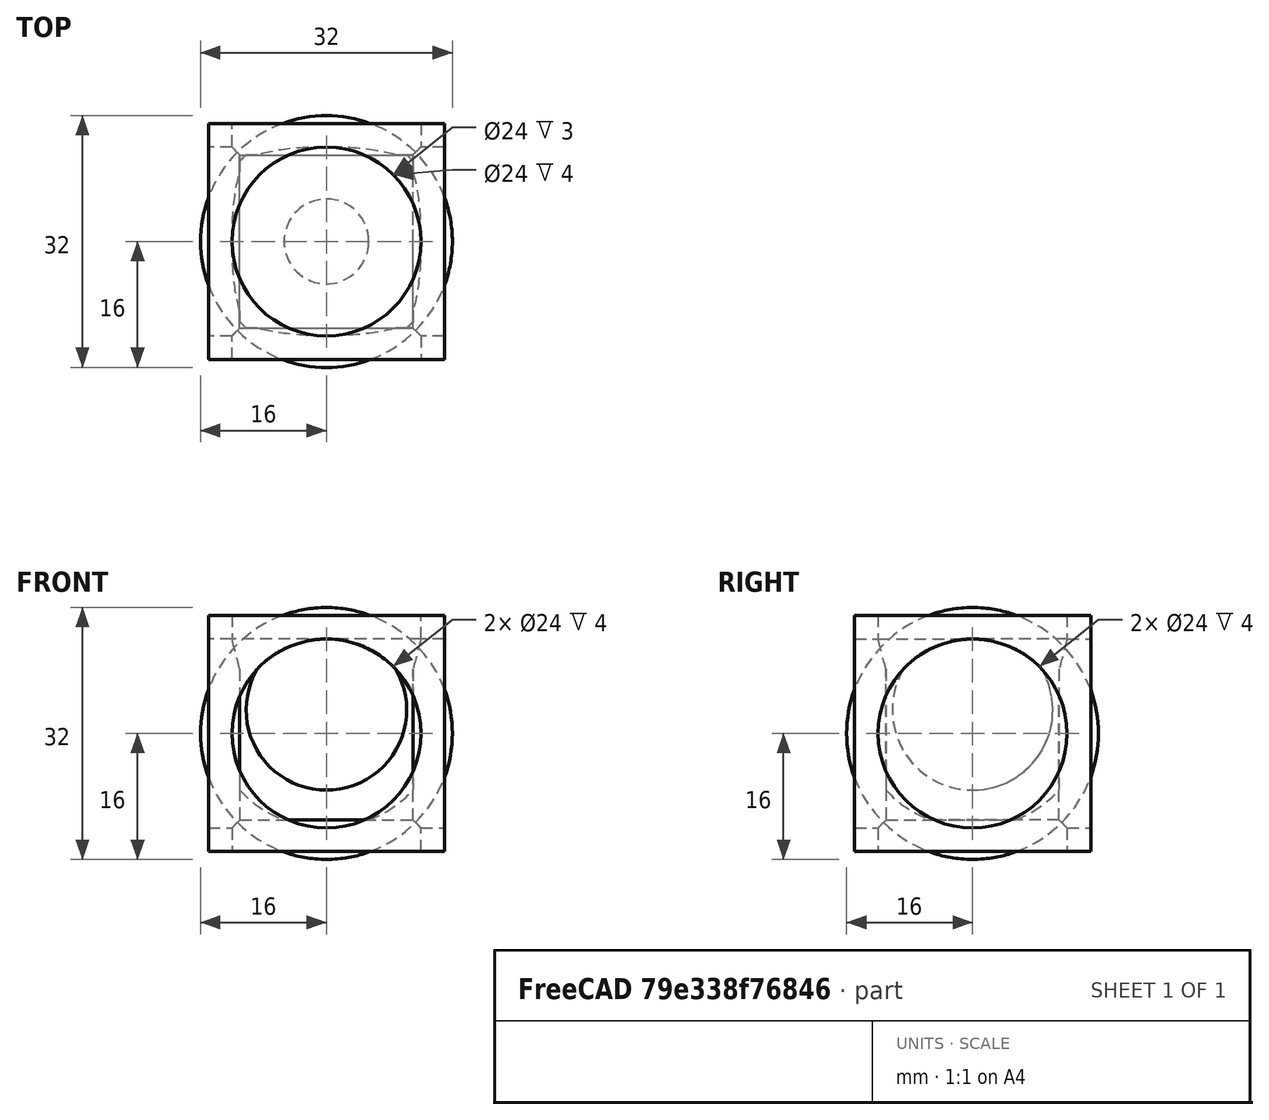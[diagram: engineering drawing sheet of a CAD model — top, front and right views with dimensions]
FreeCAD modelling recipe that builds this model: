
FCSTD DOCUMENT  (FreeCAD 0.20R29603 (Git))
Label: Ielkadi_repte3
License: All rights reserved
LicenseURL: http://en.wikipedia.org/wiki/All_rights_reserved
objects: Part::Cut×7, Part::Cylinder×6, Part::Sphere×2, Part::Box×1
note: 16 computed .brp shape members not serialized (recipe doc carries the construction recipe); baked Part::Feature solids carry a one-line shape summary decoded from their .brp

FEATURE [Part::Box] Box  label="Cub"
  AttacherType = Attacher::AttachEngine3D
  Height = 30
  Length = 30
  Width = 30
FEATURE [Part::Cylinder] Cylinder  label="Tall1"
  Angle = 360
  AttacherType = Attacher::AttachEngine3D
  FirstAngle = 0
  Height = 5
  Placement = pos=(15,15,26) rot=(0,0,1;0rad)
  Radius = 12
  SecondAngle = 0
FEATURE [Part::Cylinder] Cylinder001  label="Tall 2"
  Angle = 360
  AttacherType = Attacher::AttachEngine3D
  FirstAngle = 0
  Height = 5
  Placement = pos=(26,15,15) rot=(0,1,0;1.5708rad)
  Radius = 12
  SecondAngle = 0
FEATURE [Part::Cylinder] Cylinder002  label="Tall 003"
  Angle = 360
  AttacherType = Attacher::AttachEngine3D
  FirstAngle = 0
  Height = 5
  Placement = pos=(-1,15,15) rot=(0,1,0;1.5708rad)
  Radius = 12
  SecondAngle = 0
FEATURE [Part::Cylinder] Cylinder003  label="Cilindre"
  Angle = 360
  AttacherType = Attacher::AttachEngine3D
  FirstAngle = 0
  Height = 5
  Placement = pos=(15,4,15) rot=(1,0,0;1.5708rad)
  Radius = 12
  SecondAngle = 0
FEATURE [Part::Cylinder] Cylinder004  label="Cilindre001"
  Angle = 360
  AttacherType = Attacher::AttachEngine3D
  FirstAngle = 0
  Height = 5
  Placement = pos=(15,31,15) rot=(1,0,0;1.5708rad)
  Radius = 12
  SecondAngle = 0
FEATURE [Part::Cylinder] Cylinder005  label="Tall002"
  Angle = 360
  AttacherType = Attacher::AttachEngine3D
  FirstAngle = 0
  Height = 5
  Placement = pos=(15,15,-1) rot=(0,0,1;0rad)
  Radius = 12
  SecondAngle = 0
FEATURE [Part::Sphere] Sphere  label="Esfera tall"
  Angle1 = -90
  Angle2 = 90
  Angle3 = 360
  AttacherType = Attacher::AttachEngine3D
  Placement = pos=(15,15,18) rot=(0,0,1;0rad)
  Radius = 15
FEATURE [Part::Cut] Cut
  Base = -> Box
  Tool = -> Sphere
FEATURE [Part::Cut] Cut001
  Base = -> Cut
  Tool = -> Cylinder
FEATURE [Part::Cut] Cut002
  Base = -> Cut001
  Tool = -> Cylinder005
FEATURE [Part::Cut] Cut003
  Base = -> Cut002
  Tool = -> Cylinder004
FEATURE [Part::Cut] Cut004
  Base = -> Cut003
  Tool = -> Cylinder003
FEATURE [Part::Cut] Cut005
  Base = -> Cut004
  Tool = -> Cylinder002
FEATURE [Part::Cut] Cut006
  Base = -> Cut005
  Tool = -> Cylinder001
FEATURE [Part::Sphere] Sphere001  label="Esfera"
  Angle1 = -90
  Angle2 = 90
  Angle3 = 360
  AttacherType = Attacher::AttachEngine3D
  Placement = pos=(15,15,15) rot=(0,0,1;0rad)
  Radius = 16
